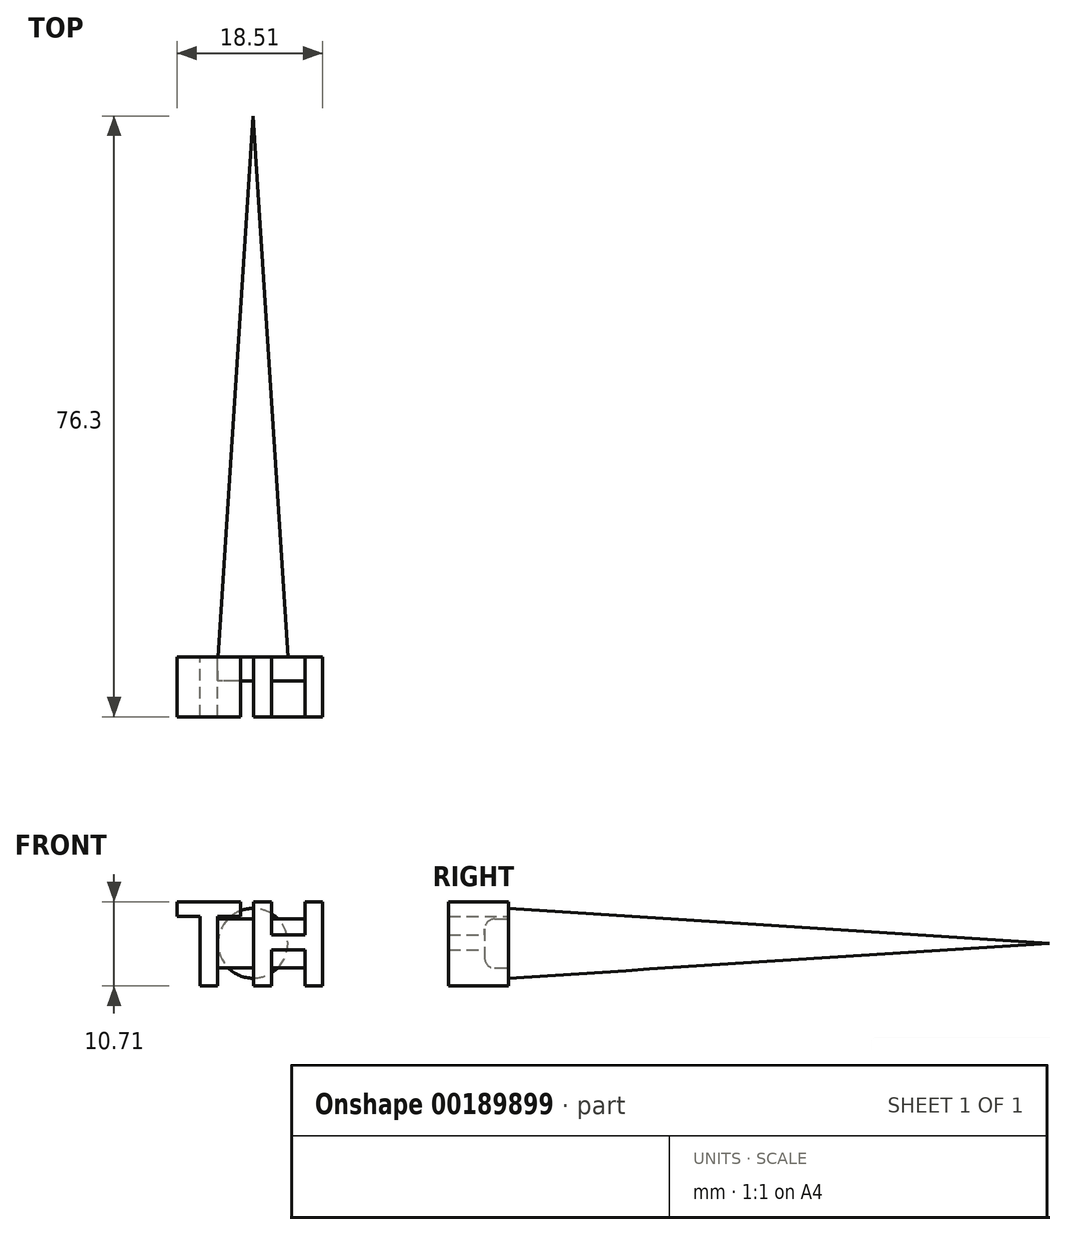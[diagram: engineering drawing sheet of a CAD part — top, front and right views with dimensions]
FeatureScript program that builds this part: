
annotation { "Feature Type Name" : "Feature", "Feature Type Description" : "" }
export const myFeature = defineFeature(function(context is Context, id is Id, definition is map)
    precondition{}
    {
        {
            var Q0;
            Q0=qCreatedBy(makeId("Front.planeOp"),FACE);
            var sketch = newSketch(context, id + "F0", { "sketchPlane" : qUnion([Q0])});
            skText(sketch, "E0", { "text": "TH", "fontName": "OpenSans-Bold.ttf"});
            const initialGuessF0  = {"E0": [-0.00996, -0.00543, 1, 0, 0.0108]};
            skSetInitialGuess(sketch, initialGuessF0);
            skSolve(sketch);
        }
        {
            var Q0;
            Q0=qSketchRegion(id+"F0",true);
            extrude(context, id + "F1", {"entities" : qUnion([Q0]), "depth" : 7.62 * mm});
        }
        {
            var Q0;
            Q0=qCreatedBy(makeId("Front.planeOp"),FACE);
            var sketch = newSketch(context, id + "F2", { "sketchPlane" : qUnion([Q0])});
            skLineSegment(sketch, "E1.bottom", {"start": v(8.14, 3.09) * mm, "end": v(-6.5, 3.09) * mm});
            skLineSegment(sketch, "E1.top", {"start": v(8.14, -3.14) * mm, "end": v(-6.5, -3.14) * mm});
            skLineSegment(sketch, "E1.left", {"start": v(8.14, 3.09) * mm, "end": v(8.14, -3.14) * mm});
            skLineSegment(sketch, "E1.right", {"start": v(-6.5, 3.09) * mm, "end": v(-6.5, -3.14) * mm});
            skSolve(sketch);
        }
        {
            var Q0;
            Q0=makeQuery(id+"F2.imprint","IMPRINT",FACE,{"disambiguationData":[TD([[makeQuery(id+"F2.imprint","IMPRINT",EDGE,{"derivedFrom":sQuery(id+"F2.wireOp",EDGE,"E1.bottom")}),1.0]])]});
            extrude(context, id + "F3", {"entities" : qUnion([Q0]), "operationType" : NewBodyOperationType.ADD, "depth" : 3.05 * mm});
        }
        {
            var Q0;
            Q0=qCreatedBy(makeId("Top.planeOp"),FACE);
            var sketch = newSketch(context, id + "F4", { "sketchPlane" : qUnion([Q0])});
            skLineSegment(sketch, "E2", {"start": v(0, 0) * mm, "end": v(0, 68.68) * mm});
            skLineSegment(sketch, "E3", {"start": v(0, 68.68) * mm, "end": v(-4.44, 0) * mm});
            skLineSegment(sketch, "E4", {"start": v(-4.44, 0) * mm, "end": v(0, 0) * mm});
            skSolve(sketch);
        }
        {
            var Q0;
            Q0=qSketchRegion(id+"F4",true);
            var Q1;
            Q1=sQuery(id+"F4.wireOp",EDGE,"E2");
            revolve(context, id + "F5", {"entities" : qUnion([Q0]), "axis" : qUnion([Q1]), "revolveType" : RevolveType.FULL});
        }
        {
            var Q0;
            Q0=makeQuery(id+"F3.opExtrude","CAP_EDGE",EDGE,{"disambiguationData":[OSD([sQuery(id+"F2.wireOp",EDGE,"E1.bottom")])],"isStart":false});
            var Q1;
            Q1=makeQuery(id+"F3.opExtrude","CAP_EDGE",EDGE,{"disambiguationData":[OSD([sQuery(id+"F2.wireOp",EDGE,"E1.top")])],"isStart":false});
            var Q2;
            Q2=makeQuery(id+"F3.opExtrude","CAP_EDGE",EDGE,{"disambiguationData":[OSD([sQuery(id+"F2.wireOp",EDGE,"E1.right")])],"isStart":false});
            var Q3;
            Q3=makeQuery(id+"F3.opExtrude","CAP_EDGE",EDGE,{"disambiguationData":[OSD([sQuery(id+"F2.wireOp",EDGE,"E1.left")])],"isStart":false});
            fillet(context, id + "F6", {"entities" : qUnion([Q0, Q1, Q2, Q3]), "radius" : 1.27 * mm, "tangentPropagation" : true, "allowEdgeOverflow" : false});
        }
    });
